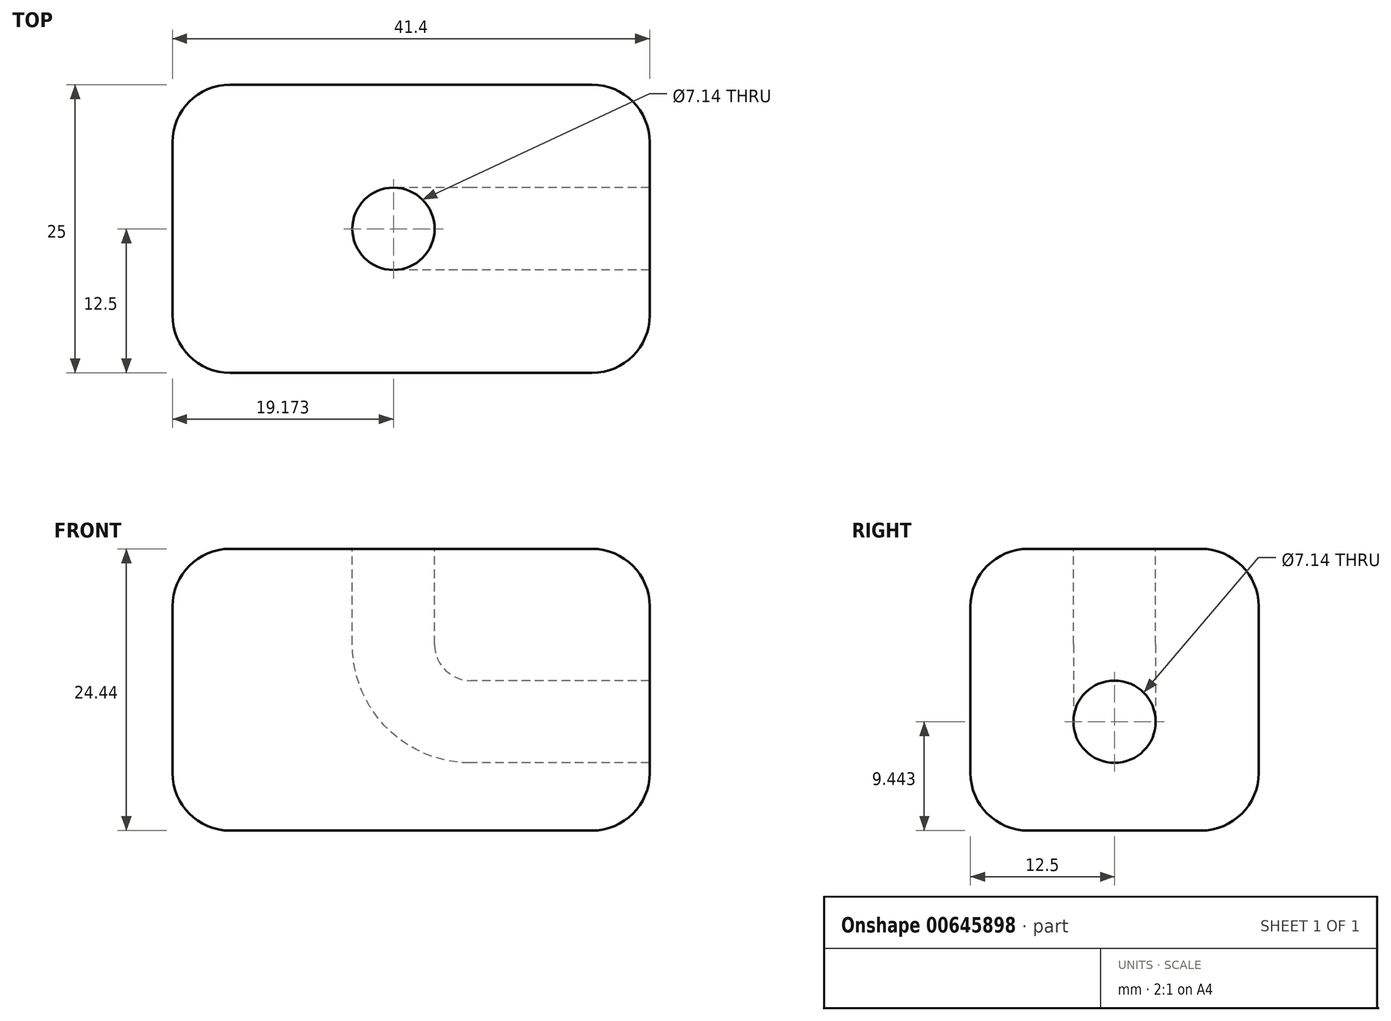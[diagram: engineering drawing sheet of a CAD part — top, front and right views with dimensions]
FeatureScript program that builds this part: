
annotation { "Feature Type Name" : "Feature", "Feature Type Description" : "" }
export const myFeature = defineFeature(function(context is Context, id is Id, definition is map)
    precondition{}
    {
        {
            var Q0;
            Q0=qCreatedBy(makeId("Front.planeOp"),FACE);
            var sketch = newSketch(context, id + "F0", { "sketchPlane" : qUnion([Q0])});
            skLineSegment(sketch, "E0.bottom", {"start": v(0, 0) * mm, "end": v(41.4, 0) * mm});
            skLineSegment(sketch, "E0.top", {"start": v(0, 24.44) * mm, "end": v(41.4, 24.44) * mm});
            skLineSegment(sketch, "E0.left", {"start": v(0, 0) * mm, "end": v(0, 24.44) * mm});
            skLineSegment(sketch, "E0.right", {"start": v(41.4, 0) * mm, "end": v(41.4, 24.44) * mm});
            skSolve(sketch);
        }
        {
            var Q0;
            Q0 = qSketchRegion(id + "F0", true);
            extrude(context, id + "F1", {"entities" : qUnion([Q0]), "depth" : 25 * mm, "offsetDistance" : 25 * mm});
        }
        {
            var Q0;
            Q0=qCreatedBy(makeId("Front.planeOp"),FACE);
            cPlane(context, id + "F2", {"entities" : qUnion([Q0]), "cplaneType" : CPlaneType.OFFSET, "offset" : 12.5 * mm, "width" : 150 * mm, "height" : 150 * mm});
        }
        {
            var Q0;
            Q0=qCreatedBy(id+"F2.planeOp",FACE);
            var sketch = newSketch(context, id + "F3", { "sketchPlane" : qUnion([Q0])});
            skLineSegment(sketch, "E1", {"start": v(41.4, 9.44) * mm, "end": v(25.88, 9.44) * mm});
            skArc(sketch, "E2", {"start": v(25.88, 9.44) * mm, "mid": v(21.14, 11.4) * mm, "end": v(19.17, 16.15) * mm});
            skLineSegment(sketch, "E3", {"start": v(19.17, 16.15) * mm, "end": v(19.17, 24.44) * mm});
            skSolve(sketch);
        }
        {
            var Q0;
            Q0=makeQuery(id+"F1.opExtrude","SWEPT_FACE",FACE,{"disambiguationData":[OSD([sQuery(id+"F0.wireOp",EDGE,"E0.right")])]});
            var sketch = newSketch(context, id + "F4", { "sketchPlane" : qUnion([Q0])});
            skCircle(sketch, "E4", {"center": v(-12.5, 9.44) * mm, "radius": 3.57 * mm});
            skSolve(sketch);
        }
        {
            var Q0;
            Q0=makeQuery(id+"F4.imprint","IMPRINT",FACE,{"disambiguationData":[TD([[makeQuery(id+"F4.imprint","IMPRINT",EDGE,{"derivedFrom":sQuery(id+"F4.wireOp",EDGE,"E4")}),1.0]])]});
            var Q1;
            Q1=sQuery(id+"F3.wireOp",EDGE,"E3");
            var Q2;
            Q2=sQuery(id+"F3.wireOp",EDGE,"E2");
            var Q3;
            Q3=sQuery(id+"F3.wireOp",EDGE,"E1");
            sweep(context, id + "F5", {"operationType" : NewBodyOperationType.REMOVE, "profiles" : qUnion([Q0]), "path" : qUnion([Q1, Q2, Q3])});
        }
        {
            var Q0;
            Q0=makeQuery(id+"F1.opExtrude","CAP_EDGE",EDGE,{"disambiguationData":[OSD([sQuery(id+"F0.wireOp",EDGE,"E0.right")])],"isStart":true});
            var Q1;
            Q1=makeQuery(id+"F1.opExtrude","CAP_EDGE",EDGE,{"disambiguationData":[OSD([sQuery(id+"F0.wireOp",EDGE,"E0.top")])],"isStart":true});
            var Q2;
            Q2=makeQuery(id+"F1.opExtrude","CAP_EDGE",EDGE,{"disambiguationData":[OSD([sQuery(id+"F0.wireOp",EDGE,"E0.left")])],"isStart":true});
            var Q3;
            Q3=makeQuery(id+"F1.opExtrude","CAP_EDGE",EDGE,{"disambiguationData":[OSD([sQuery(id+"F0.wireOp",EDGE,"E0.bottom")])],"isStart":true});
            var Q4;
            Q4=makeQuery(id+"F1.opExtrude","CAP_EDGE",EDGE,{"disambiguationData":[OSD([sQuery(id+"F0.wireOp",EDGE,"E0.right")])],"isStart":false});
            var Q5;
            Q5=makeQuery(id+"F1.opExtrude","CAP_EDGE",EDGE,{"disambiguationData":[OSD([sQuery(id+"F0.wireOp",EDGE,"E0.top")])],"isStart":false});
            var Q6;
            Q6=makeQuery(id+"F1.opExtrude","CAP_EDGE",EDGE,{"disambiguationData":[OSD([sQuery(id+"F0.wireOp",EDGE,"E0.left")])],"isStart":false});
            var Q7;
            Q7=makeQuery(id+"F1.opExtrude","CAP_EDGE",EDGE,{"disambiguationData":[OSD([sQuery(id+"F0.wireOp",EDGE,"E0.bottom")])],"isStart":false});
            var Q8;
            Q8=makeQuery(id+"F1.opExtrude","SWEPT_EDGE",EDGE,{"disambiguationData":[OSD([sQuery(id+"F0.wireOp",EDGE,"E0.bottom"),sQuery(id+"F0.wireOp",EDGE,"E0.right")])]});
            var Q9;
            Q9=makeQuery(id+"F1.opExtrude","SWEPT_EDGE",EDGE,{"disambiguationData":[OSD([sQuery(id+"F0.wireOp",EDGE,"E0.bottom"),sQuery(id+"F0.wireOp",EDGE,"E0.left")])]});
            var Q10;
            Q10=makeQuery(id+"F1.opExtrude","SWEPT_EDGE",EDGE,{"disambiguationData":[OSD([sQuery(id+"F0.wireOp",EDGE,"E0.top"),sQuery(id+"F0.wireOp",EDGE,"E0.right")])]});
            var Q11;
            Q11=makeQuery(id+"F1.opExtrude","SWEPT_EDGE",EDGE,{"disambiguationData":[OSD([sQuery(id+"F0.wireOp",EDGE,"E0.top"),sQuery(id+"F0.wireOp",EDGE,"E0.left")])]});
            fillet(context, id + "F6", {"entities" : qUnion([Q0, Q1, Q2, Q3, Q4, Q5, Q6, Q7, Q8, Q9, Q10, Q11]), "radius" : 5 * mm, "tangentPropagation" : true, "allowEdgeOverflow" : false});
        }
    });
